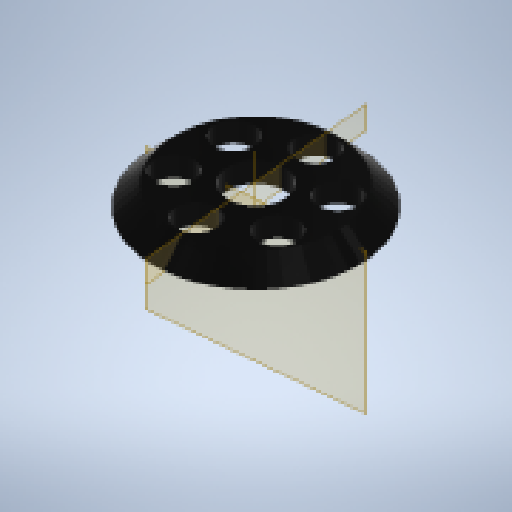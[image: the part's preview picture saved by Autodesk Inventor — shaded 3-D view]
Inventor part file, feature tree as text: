
AUTODESK INVENTOR PART (.ipt)
format: ipt  version: 2023 (Build 270158000, 158)  size: 277,504 bytes
history: native  units: in
note: dims shown in document units (in); Inventor stores cm internally (conversion verified against a paired STEP export)
features: other x5, plane x3
ambient origin geometry x8: Origin, YZ Plane, XZ Plane, XY Plane, X Axis, Y Axis, Z Axis, Center Point
feature tree (8):
  other  "SkittlesHopperInsertV3.2"
  plane  "Work Plane2"
  plane  "Work Plane3"
  other  "Work Axis1"
  plane  "Work Plane1"
  other  "MeshFeature1"
  other  "Skittles Hopper Assembly.iam"
  other  "main Hopper body v6:1"
